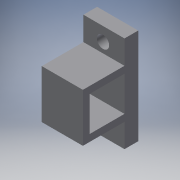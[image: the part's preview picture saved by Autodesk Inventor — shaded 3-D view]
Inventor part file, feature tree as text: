
AUTODESK INVENTOR PART (.ipt)
format: ipt  version: 2019.3 (Build 233278000, 278)  size: 118,272 bytes
history: native  units: mm
features: reference x12, other x6, sketch x2, extrude x2, plane x1
ambient origin geometry x8: Origin, YZ Plane, XZ Plane, XY Plane, X Axis, Y Axis, Z Axis, Center Point
bodies: Solid1 (feature_tree)
feature tree (23):
  sketch  "Sketch1"  dims[d0=10.0mm d1=0.0mm d2=10.0mm d3=0.0mm]
  plane  "Work Plane1"
  extrude  "Extrusion1"  Depth=10.0mm TaperAngle=0.0deg
  extrude  "Extrusion2"  [1 undecoded]
  reference  "Reference1"
  reference  "Reference2"
  reference  "Reference3"
  reference  "Reference4"
  reference  "Reference5"
  reference  "Reference6"
  sketch  "Sketch2"
  reference  "Reference8"
  reference  "Reference9"
  reference  "Reference10"
  reference  "Reference11"
  reference  "Reference12"
  reference  "Reference13"
  parser-record x1  (decoder bookkeeping rows leaked as tree rows — omitted from the tree; the rows remain in map.json)
  other  "Assembly.iam"
  other  "CameraBracket:1"
  other  "RailMount:1"
  other  "CornerBracket:2"
  other  "LateralBars:1"
note: 1 required parameter value undecoded (feature->parameter linkage not recoverable at this tier; creation-order binding heuristic only, values carry confidence <= 0.55)
note: 1 file-system path scrubbed to <path> (originals preserved in map.json)
